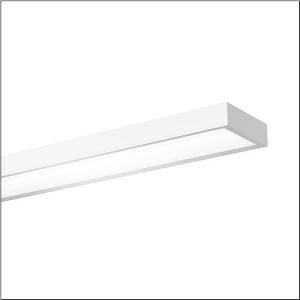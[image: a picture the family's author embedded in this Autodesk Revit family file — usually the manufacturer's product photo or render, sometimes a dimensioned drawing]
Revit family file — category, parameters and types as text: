
# Revit family: sport_31_51hs12dc4dca
name_source: partatom
category: Lighting Fixtures
units: mm (PartAtom-declared; Revit-internal decimal feet)

## family parameters
Cut with Voids When Loaded = No
Host = Face
Light Source = No
Part Type = Normal
Room Calculation Point = No
Round Connector Dimension = Use Diameter
Shared = No

## types (1)
- --- (1 x LED, 8000 lm, 59.4 W, 4000K)
    Apparent Load = 59 VA
    CIE Flux Codes = 65 89 97 100 100
    Color Rendering = 80
    Color Temperature = 4000K
    Default Elevation = 1800 mm
    Description = Sport 31, high bay luminaire, primary light control with reflector, of sheet steel, primary anti-glare with prismatic structure, of PC, primary optical cover: cover panel, of PC, light emission: direct distribution, primary light characteristic: symmetric, installation type: suspended mounting, recessed, surface-mounted, LED, rated luminous flux: 8.000lm, luminous efficacy: 135lm/W, light colour: 840, colour temperature: 4000K, control gear: DALI 2, with terminal, 5-pole, max. 2.5mm², mains connection: 220..240V, AC/DC, 50/60Hz, rated input power: 58W, housing, of sheet steel, traffic white (RAL 9016), length: 1.540mm, width: 315mm, height: 95mm, protection rating (complete): IP20, protection rating (lamp compartment, on room side): IP50, insulation class (complete): insulation class I (protective earthing), certification: CE, ENEC, UKCA, ball protection: ball impact resistant with ceiling mounting or chain suspension, impact resistance: IK08, permissible operating ambient temperature: -20..+35°C, standard: DIN 18032-3, EN 60598-2-22, packaging unit: 1 piece
    Height = 100 mm  [stored 0.328084 ft]
    Lamp = 1 x LED
    Lamp Light Flux = 8000 lm
    Lamp Power = 59.4 W
    Lamp count = 1
    Length = 1500 mm
    Luminous efficacy = 135 lm/W
    Manufacturer = Siteco
    ModVariant = No
    Model = 51HS12DC4DCA
    Mounting Place = Ceiling
    Mounting Type = Pendant
    Number of Poles = 1
    OnlyDefault = Yes
    Power Factor = 1
    Product Name = Sport 31
    Product group = high bay luminaire
    ProductGroupID = 902
    Protection Class = Protection class I
    Protection Degree = IP 20
    RLX_Detail_Level = 1
    RLX_Emergency_Light_Flux = 0 lm
    RLX_Emergency_Type = 0
    RLX_Emergency_Type_DB = No
    RlxData = <blob elided: 22765 chars, md5=1db292bf>
    Socket = socket
    Standby Power = 0 W
    System Light Flux = 8000 lm
    System Power = 59 W
    Type Comments = factory setting: luminous flux: 100 % | dim-lin: 254 | 247 mA
    Type Image = l_1397489.jpg
    URL = http://relux.com
    VarID = @adj_196249
    Voltage = 0 V
    Weight = 0.00 kg
    Width = 315 mm

note: [stored X ft] marks values corroborated as IEEE doubles in the binary element streams (Revit-internal decimal feet)

## geometry (parser evidence)
native form markers: Blend x4, Sweep x11
no freeform markers — native parametric forms only
